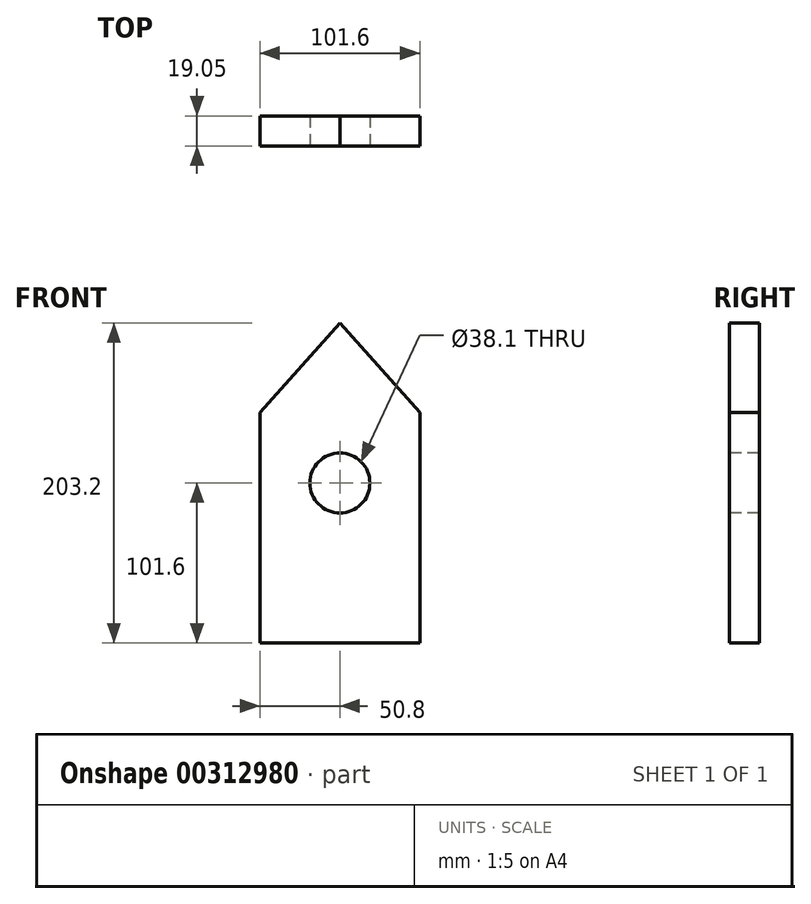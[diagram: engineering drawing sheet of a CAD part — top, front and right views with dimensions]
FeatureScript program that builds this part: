
annotation { "Feature Type Name" : "Feature", "Feature Type Description" : "" }
export const myFeature = defineFeature(function(context is Context, id is Id, definition is map)
    precondition{}
    {
        {
            var Q0;
            Q0=qCreatedBy(makeId("Front.planeOp"),FACE);
            var sketch = newSketch(context, id + "F0", { "sketchPlane" : qUnion([Q0])});
            skLineSegment(sketch, "E0.bottom", {"start": v(50.8, 101.6) * mm, "end": v(-50.8, 101.6) * mm});
            skLineSegment(sketch, "E0.top", {"start": v(50.8, -101.6) * mm, "end": v(-50.8, -101.6) * mm});
            skLineSegment(sketch, "E0.left", {"start": v(50.8, 101.6) * mm, "end": v(50.8, -101.6) * mm});
            skLineSegment(sketch, "E0.right", {"start": v(-50.8, 101.6) * mm, "end": v(-50.8, -101.6) * mm});
            skPoint(sketch, "E0.middle", {"position": v(0, 0) * mm});
            skSolve(sketch);
        }
        {
            var Q0;
            Q0 = qSketchRegion(id + "F0", true);
            extrude(context, id + "F1", {"entities" : qUnion([Q0]), "depth" : 19.05 * mm});
        }
        {
            var Q0;
            Q0=makeQuery(id+"F1.opExtrude","CAP_FACE",FACE,{"disambiguationData":[OSD([sQuery(id+"F0.wireOp",EDGE,"E0.bottom"),sQuery(id+"F0.wireOp",EDGE,"E0.top"),sQuery(id+"F0.wireOp",EDGE,"E0.left"),sQuery(id+"F0.wireOp",EDGE,"E0.right")])],"isStart":false});
            var sketch = newSketch(context, id + "F2", { "sketchPlane" : qUnion([Q0])});
            skLineSegment(sketch, "E1", {"start": v(0, 101.6) * mm, "end": v(-50.8, 44.8) * mm});
            skLineSegment(sketch, "E2", {"start": v(0, 101.6) * mm, "end": v(50.8, 44.8) * mm});
            skSolve(sketch);
        }
        {
            var Q0;
            Q0 = qSketchRegion(id + "F2", true);
            var Q1;
            {var subQ0=sQuery(id+"F2.wireOp",EDGE,"SVPoMazK-Gu85-GyVv-sP3m-4TBhHXVYDlBG");Q1=makeQuery(id+"F2.imprint","IMPRINT",FACE,{"disambiguationData":[TD([[makeQuery(id+"F2.imprint","IMPRINT",EDGE,{"derivedFrom":subQ0}),-1.0]])]});}
            var Q2;
            {var subQ0=sQuery(id+"F2.wireOp",EDGE,"VwRt71yy-8RgG-NqiF-pPwH-gTAyYK7ToVJU");Q2=makeQuery(id+"F2.imprint","IMPRINT",FACE,{"disambiguationData":[TD([[makeQuery(id+"F2.imprint","IMPRINT",EDGE,{"derivedFrom":subQ0}),1.0]])]});}
            var Q3;
            {var subQ0=sQuery(id+"F2.wireOp",EDGE,"E1");Q3=makeQuery(id+"F2.imprint","IMPRINT",FACE,{"disambiguationData":[TD([[makeQuery(id+"F2.imprint","IMPRINT",EDGE,{"derivedFrom":subQ0}),-1.0]])]});}
            var Q4;
            {var subQ0=sQuery(id+"F2.wireOp",EDGE,"E2");Q4=makeQuery(id+"F2.imprint","IMPRINT",FACE,{"disambiguationData":[TD([[makeQuery(id+"F2.imprint","IMPRINT",EDGE,{"derivedFrom":subQ0}),1.0]])]});}
            extrude(context, id + "F3", {"entities" : qUnion([Q0, Q1, Q2, Q3, Q4]), "operationType" : NewBodyOperationType.REMOVE, "endBound" : BoundingType.THROUGH_ALL, "oppositeDirection" : true, "depth" : 25.4 * mm});
        }
        {
            var Q0;
            Q0=makeQuery(id+"F1.opExtrude","CAP_FACE",FACE,{"disambiguationData":[OSD([sQuery(id+"F0.wireOp",EDGE,"E0.bottom"),sQuery(id+"F0.wireOp",EDGE,"E0.top"),sQuery(id+"F0.wireOp",EDGE,"E0.left"),sQuery(id+"F0.wireOp",EDGE,"E0.right")])],"isStart":false});
            var sketch = newSketch(context, id + "F4", { "sketchPlane" : qUnion([Q0])});
            skCircle(sketch, "E3", {"center": v(0, 0) * mm, "radius": 19.05 * mm});
            skSolve(sketch);
        }
        {
            var Q0;
            Q0 = qSketchRegion(id + "F4", true);
            extrude(context, id + "F5", {"entities" : qUnion([Q0]), "operationType" : NewBodyOperationType.REMOVE, "endBound" : BoundingType.THROUGH_ALL, "oppositeDirection" : true, "depth" : 25.4 * mm});
        }
    });
